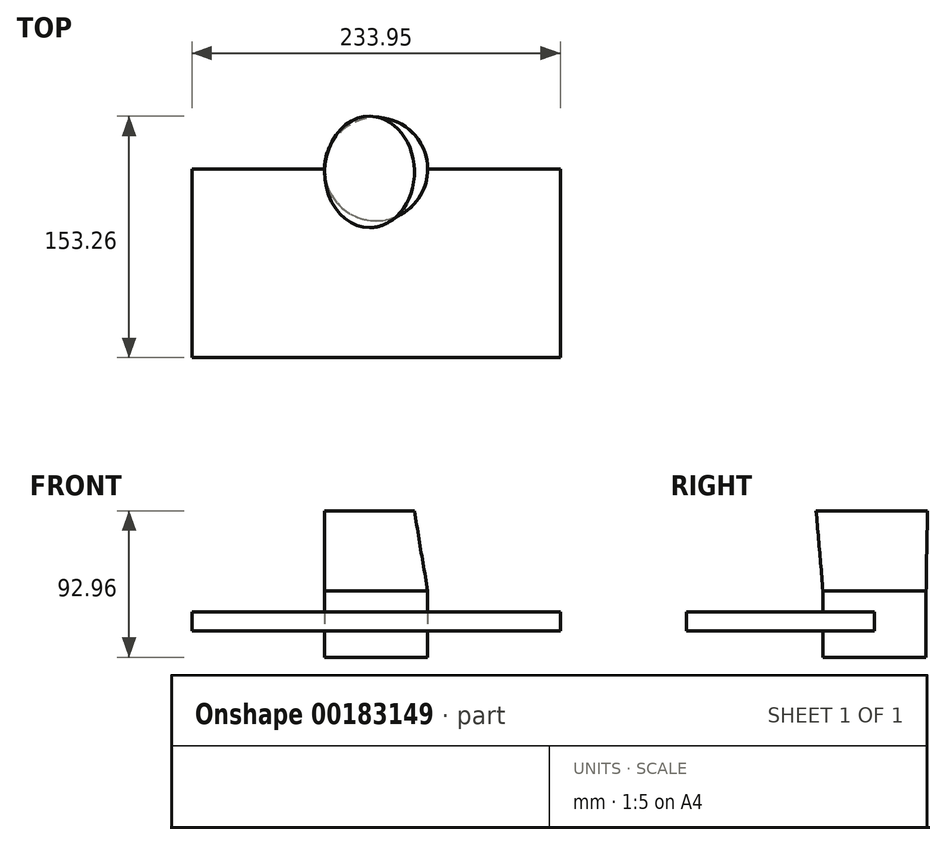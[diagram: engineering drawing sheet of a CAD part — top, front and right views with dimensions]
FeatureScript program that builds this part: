
annotation { "Feature Type Name" : "Feature", "Feature Type Description" : "" }
export const myFeature = defineFeature(function(context is Context, id is Id, definition is map)
    precondition{}
    {
        {
            var Q0;
            Q0=qCreatedBy(makeId("Top.planeOp"),FACE);
            var sketch = newSketch(context, id + "F0", { "sketchPlane" : qUnion([Q0])});
            skLineSegment(sketch, "E0.bottom", {"start": v(-116.52, 44.68) * mm, "end": v(117.43, 44.68) * mm});
            skLineSegment(sketch, "E0.top", {"start": v(-116.52, -74.9) * mm, "end": v(117.43, -74.9) * mm});
            skLineSegment(sketch, "E0.left", {"start": v(-116.52, 44.68) * mm, "end": v(-116.52, -74.9) * mm});
            skLineSegment(sketch, "E0.right", {"start": v(117.43, 44.68) * mm, "end": v(117.43, -74.9) * mm});
            skCircle(sketch, "E1", {"center": v(0.45, 44.68) * mm, "radius": 32.77 * mm});
            skSolve(sketch);
        }
        {
            var Q0;
            Q0=makeQuery(id+"F0.imprint","IMPRINT",FACE,{"disambiguationData":[TD([[makeQuery(id+"F0.imprint","IMPRINT",EDGE,{"derivedFrom":sQuery(id+"F0.wireOp",EDGE,"E0.top")}),1.0]])]});
            var Q1;
            Q1=sQuery(id+"F0.wireOp",EDGE,"E0.left");
            extrude(context, id + "F1", {"entities" : qUnion([Q0]), "surfaceEntities" : qUnion([Q1]), "depth" : 11.94 * mm});
        }
        {
            var Q0;
            {var subQ0=sQuery(id+"F0.wireOp",EDGE,"E1");var subQ1=sQuery(id+"F0.wireOp",EDGE,"E0.bottom");var subQ2=makeQuery(id+"F0.imprint","INTERSECT",VERTEX,{"disambiguationData":[OD(0.0)],"derivedFrom":[subQ1,subQ0]});Q0=makeQuery(id+"F0.imprint","IMPRINT",FACE,{"disambiguationData":[TD([[makeQuery(id+"F0.imprint","IMPRINT",EDGE,{"disambiguationData":[TD([[subQ2,-1.0]])],"derivedFrom":subQ1}),1.0]])]});}
            var Q1;
            {var subQ0=sQuery(id+"F0.wireOp",EDGE,"E1");var subQ1=sQuery(id+"F0.wireOp",EDGE,"E0.bottom");var subQ2=makeQuery(id+"F0.imprint","INTERSECT",VERTEX,{"disambiguationData":[OD(0.0)],"derivedFrom":[subQ1,subQ0]});Q1=makeQuery(id+"F0.imprint","IMPRINT",FACE,{"disambiguationData":[TD([[makeQuery(id+"F0.imprint","IMPRINT",EDGE,{"disambiguationData":[TD([[subQ2,-1.0]])],"derivedFrom":subQ1}),-1.0]])]});}
            extrude(context, id + "F2", {"entities" : qUnion([Q0, Q1]), "operationType" : NewBodyOperationType.ADD, "depth" : 25.4 * mm, "hasSecondDirection" : true, "secondDirectionOppositeDirection" : true, "secondDirectionDepth" : 16.76 * mm});
        }
        {
            var Q0;
            Q0=makeQuery(id+"F2.opExtrude","CAP_FACE",FACE,{"disambiguationData":[OSD([sQuery(id+"F0.wireOp",EDGE,"E1")])],"isStart":false});
            cPlane(context, id + "F3", {"entities" : qUnion([Q0]), "cplaneType" : CPlaneType.OFFSET, "offset" : 50.8 * mm, "width" : 152.4 * mm, "height" : 152.4 * mm});
        }
        {
            var Q0;
            Q0=qCreatedBy(id+"F3.planeOp",FACE);
            var sketch = newSketch(context, id + "F4", { "sketchPlane" : qUnion([Q0])});
            skEllipse(sketch, "E2", {"center": v(-3.68, 42.97) * mm, "majorRadius": 28.49 * mm, "minorRadius": 35.38 * mm, "majorAxis": v(-1, 0)});
            skSolve(sketch);
        }
        {
            var Q0;
            Q0=makeQuery(id+"F4.imprint","IMPRINT",FACE,{"disambiguationData":[TD([[makeQuery(id+"F4.imprint","IMPRINT",EDGE,{"derivedFrom":sQuery(id+"F4.wireOp",EDGE,"E2")}),1.0]])]});
            var Q1;
            Q1=makeQuery(id+"F2.opExtrude","CAP_FACE",FACE,{"disambiguationData":[OSD([sQuery(id+"F0.wireOp",EDGE,"E1")])],"isStart":false});
            loft(context, id + "F5", {"sheetProfilesArray" : [{ "sheetProfileEntities" : qUnion([Q0]) }, { "sheetProfileEntities" : qUnion([Q1]) }]});
        }
    });
